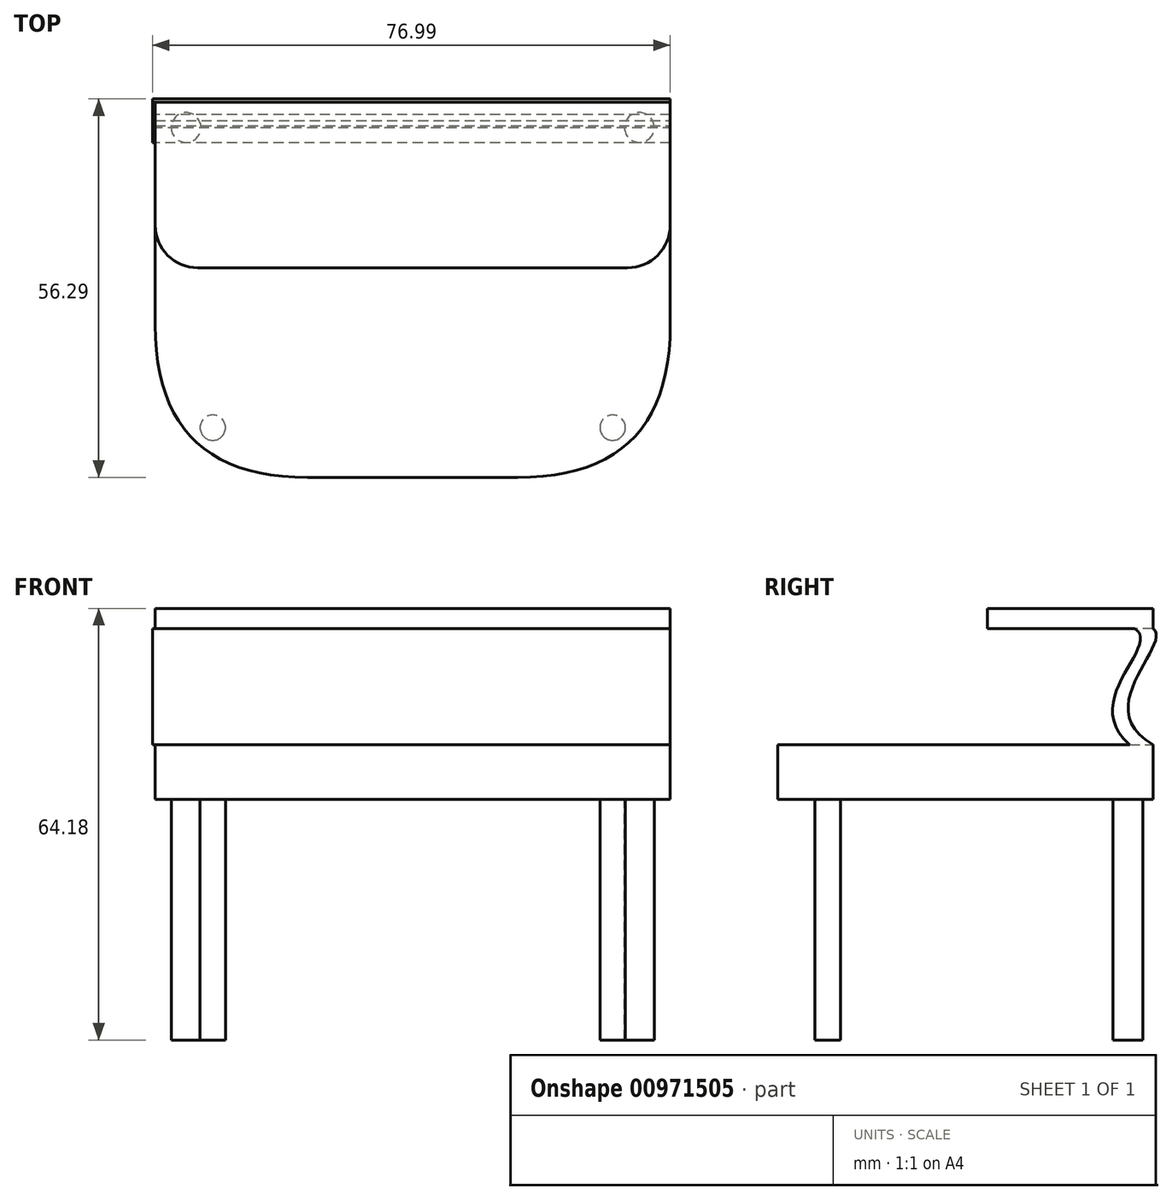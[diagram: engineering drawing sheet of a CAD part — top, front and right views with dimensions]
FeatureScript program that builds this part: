
annotation { "Feature Type Name" : "Feature", "Feature Type Description" : "" }
export const myFeature = defineFeature(function(context is Context, id is Id, definition is map)
    precondition{}
    {
        {
            var Q0;
            Q0=qCreatedBy(makeId("Top.planeOp"),FACE);
            var sketch = newSketch(context, id + "F0", { "sketchPlane" : qUnion([Q0])});
            skLineSegment(sketch, "E0.bottom", {"start": v(0, 0) * mm, "end": v(-76.58, 0) * mm});
            skLineSegment(sketch, "E0.top", {"start": v(0, 55.8) * mm, "end": v(-76.58, 55.8) * mm});
            skLineSegment(sketch, "E0.left", {"start": v(0, 0) * mm, "end": v(0, 55.8) * mm});
            skLineSegment(sketch, "E0.right", {"start": v(-76.58, 0) * mm, "end": v(-76.58, 55.8) * mm});
            skSolve(sketch);
        }
        {
            var Q0;
            Q0=makeQuery(id+"F0.imprint","IMPRINT",FACE,{"disambiguationData":[TD([[makeQuery(id+"F0.imprint","IMPRINT",EDGE,{"derivedFrom":sQuery(id+"F0.wireOp",EDGE,"E0.bottom")}),-1.0]])]});
            cPlane(context, id + "F1", {"entities" : qUnion([Q0]), "cplaneType" : CPlaneType.OFFSET, "offset" : 25.4 * mm, "width" : 152.4 * mm, "height" : 152.4 * mm});
        }
        {
            var Q0;
            Q0 = qSketchRegion(id + "F0", true);
            extrude(context, id + "F2", {"entities" : qUnion([Q0]), "depth" : 8.13 * mm, "offsetDistance" : 25.4 * mm});
        }
        {
            var Q0;
            Q0=qCreatedBy(id+"F1.planeOp",FACE);
            var sketch = newSketch(context, id + "F3", { "sketchPlane" : qUnion([Q0])});
            skLineSegment(sketch, "E1.0.0", {"start": v(0, 37.53) * mm, "end": v(0, 55.8) * mm});
            skLineSegment(sketch, "E1.0.1", {"start": v(0, 55.8) * mm, "end": v(-76.58, 55.8) * mm});
            skLineSegment(sketch, "E1.0.2", {"start": v(-76.58, 55.8) * mm, "end": v(-76.58, 37.53) * mm});
            skLineSegment(sketch, "E2", {"start": v(-70.23, 31.18) * mm, "end": v(-6.35, 31.18) * mm});
            skPoint(sketch, "E3.visualSharp", {"position": v(-76.58, 31.18) * mm});
            skArc(sketch, "E3.filletArc", {"start": v(-76.58, 37.53) * mm, "mid": v(-74.72, 33.04) * mm, "end": v(-70.23, 31.18) * mm});
            skPoint(sketch, "E4.visualSharp", {"position": v(0, 31.18) * mm});
            skArc(sketch, "E4.filletArc", {"start": v(-6.35, 31.18) * mm, "mid": v(-1.86, 33.04) * mm, "end": v(0, 37.53) * mm});
            skSolve(sketch);
        }
        {
            var Q0;
            Q0 = qSketchRegion(id + "F3", true);
            extrude(context, id + "F4", {"entities" : qUnion([Q0]), "depth" : 2.97 * mm, "offsetDistance" : 25.4 * mm});
        }
        {
            var Q0;
            Q0=qCreatedBy(makeId("Right.planeOp"),FACE);
            var sketch = newSketch(context, id + "F5", { "sketchPlane" : qUnion([Q0])});
            skLineSegment(sketch, "E5.0.0", {"start": v(55.8, 25.4) * mm, "end": v(53.1, 25.4) * mm});
            skLineSegment(sketch, "E6.0.2", {"start": v(52.33, 8.13) * mm, "end": v(55.8, 8.13) * mm});
            skFitSpline(sketch, "E7", {"points": [v(55.8, 25.4) * mm, v(55.8, 8.13) * mm], "startDerivative": vector(9.12, -6.8) * mm, "endDerivative": vector(29.17, -16.35) * mm});
            skFitSpline(sketch, "E8", {"points": [v(53.1, 25.4) * mm, v(52.33, 8.13) * mm], "startDerivative": vector(12.2, -7.9) * mm, "endDerivative": vector(23.13, -20.07) * mm});
            skPoint(sketch, "E5.0.1.end.orphan", {"position": v(37.53, 28.37) * mm});
            skPoint(sketch, "E9.orphan", {"position": v(37.53, 25.4) * mm});
            skPoint(sketch, "E5.0.3.start.orphan", {"position": v(55.8, 28.37) * mm});
            skPoint(sketch, "E6.0.0.end.orphan", {"position": v(0, 0) * mm});
            skPoint(sketch, "E10.orphan", {"position": v(0, 8.13) * mm});
            skPoint(sketch, "E6.0.3.end.orphan", {"position": v(55.8, 0) * mm});
            skSolve(sketch);
        }
        {
            var Q0;
            Q0 = qSketchRegion(id + "F5", true);
            extrude(context, id + "F6", {"entities" : qUnion([Q0]), "operationType" : NewBodyOperationType.ADD, "oppositeDirection" : true, "depth" : 76.99 * mm, "offsetDistance" : 25.4 * mm});
        }
        {
            var Q0;
            Q0=makeQuery(id+"F2.opExtrude","SWEPT_EDGE",EDGE,{"disambiguationData":[OSD([sQuery(id+"F0.wireOp",EDGE,"E0.bottom"),sQuery(id+"F0.wireOp",EDGE,"E0.right")])]});
            var Q1;
            Q1=makeQuery(id+"F2.opExtrude","SWEPT_EDGE",EDGE,{"disambiguationData":[OSD([sQuery(id+"F0.wireOp",EDGE,"E0.bottom"),sQuery(id+"F0.wireOp",EDGE,"E0.left")])]});
            fillet(context, id + "F7", {"entities" : qUnion([Q0, Q1]), "radius" : 22.7 * mm, "tangentPropagation" : true, "rho" : 0.5, "crossSection" : FilletCrossSection.CONIC, "allowEdgeOverflow" : false});
        }
        {
            var Q0;
            Q0=makeQuery(id+"F2.opExtrude","CAP_FACE",FACE,{"disambiguationData":[OSD([sQuery(id+"F0.wireOp",EDGE,"E0.bottom"),sQuery(id+"F0.wireOp",EDGE,"E0.top"),sQuery(id+"F0.wireOp",EDGE,"E0.left"),sQuery(id+"F0.wireOp",EDGE,"E0.right")])],"isStart":true});
            var sketch = newSketch(context, id + "F8", { "sketchPlane" : qUnion([Q0])});
            skLineSegment(sketch, "E11", {"start": v(-38.3, 0) * mm, "end": v(-38.3, -55.8) * mm, "construction": true});
            skPoint(sketch, "E11.endSnap0", {"position": v(-38.3, -55.8) * mm});
            skCircle(sketch, "E12", {"center": v(-72, -52.05) * mm, "radius": 2.21 * mm});
            skCircle(sketch, "E13", {"center": v(-68.02, -7.4) * mm, "radius": 1.89 * mm});
            skCircle(sketch, "E14.MirrorC", {"center": v(-4.59, -52.05) * mm, "radius": 2.21 * mm});
            skCircle(sketch, "E15.MirrorC", {"center": v(-8.56, -7.4) * mm, "radius": 1.89 * mm});
            skSolve(sketch);
        }
        {
            var Q0;
            Q0 = qSketchRegion(id + "F8", true);
            extrude(context, id + "F9", {"entities" : qUnion([Q0]), "operationType" : NewBodyOperationType.ADD, "depth" : 35.81 * mm, "offsetDistance" : 25.4 * mm});
        }
    });
